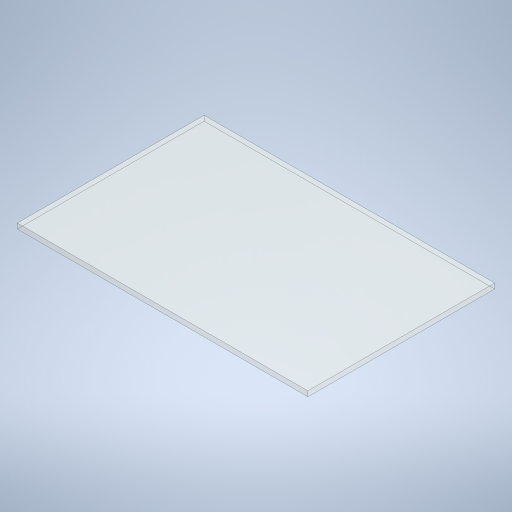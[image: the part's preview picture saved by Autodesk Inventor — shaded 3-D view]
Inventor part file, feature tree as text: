
AUTODESK INVENTOR PART (.ipt)
format: ipt  version: 2024 (Build 280153000, 153)  size: 222,208 bytes
history: native  units: in
note: dims shown in document units (in); Inventor stores cm internally (conversion verified against a paired STEP export)
features: extrude x1, sketch x1
ambient origin geometry x8: Origin, YZ Plane, XZ Plane, XY Plane, X Axis, Y Axis, Z Axis, Center Point
bodies: Solid1 (feature_tree)
feature tree (2):
  extrude  "Extrusion1"  Depth=9.0in
  sketch  "Sketch1"  dims[d0=14.0in d1=9.0in d2=0.25in d3=0.0in]
